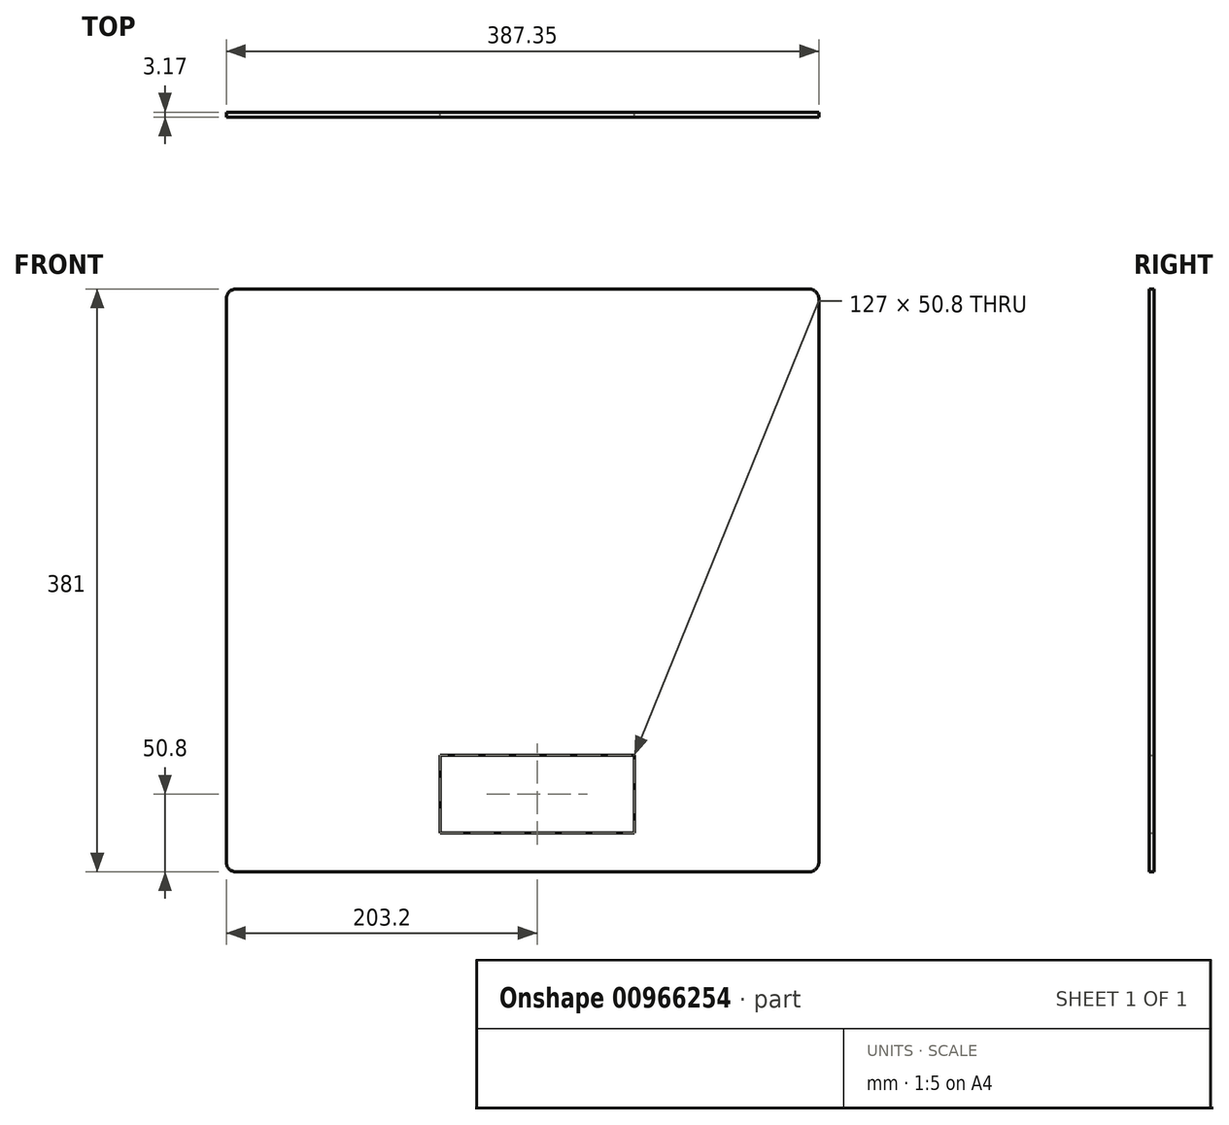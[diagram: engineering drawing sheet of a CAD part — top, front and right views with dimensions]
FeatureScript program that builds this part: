
annotation { "Feature Type Name" : "Feature", "Feature Type Description" : "" }
export const myFeature = defineFeature(function(context is Context, id is Id, definition is map)
    precondition{}
    {
        {
            var Q0;
            Q0=qCreatedBy(makeId("Front.planeOp"),FACE);
            var sketch = newSketch(context, id + "F0", { "sketchPlane" : qUnion([Q0])});
            skLineSegment(sketch, "E0.bottom", {"start": v(6.35, 0) * mm, "end": v(381, 0) * mm});
            skLineSegment(sketch, "E0.top", {"start": v(6.35, 381) * mm, "end": v(381, 381) * mm});
            skLineSegment(sketch, "E0.left", {"start": v(0, 6.35) * mm, "end": v(0, 374.65) * mm});
            skLineSegment(sketch, "E0.right", {"start": v(387.35, 6.35) * mm, "end": v(387.35, 374.65) * mm});
            skPoint(sketch, "E1.visualSharp", {"position": v(0, 381) * mm});
            skArc(sketch, "E1.filletArc", {"start": v(6.35, 381) * mm, "mid": v(1.86, 379.14) * mm, "end": v(0, 374.65) * mm});
            skPoint(sketch, "E2.visualSharp", {"position": v(0, 0) * mm});
            skArc(sketch, "E2.filletArc", {"start": v(0, 6.35) * mm, "mid": v(1.86, 1.86) * mm, "end": v(6.35, 0) * mm});
            skPoint(sketch, "E3.visualSharp", {"position": v(387.35, 0) * mm});
            skArc(sketch, "E3.filletArc", {"start": v(381, 0) * mm, "mid": v(385.5, 1.86) * mm, "end": v(387.35, 6.35) * mm});
            skPoint(sketch, "E4.visualSharp", {"position": v(387.35, 381) * mm});
            skArc(sketch, "E4.filletArc", {"start": v(387.35, 374.65) * mm, "mid": v(385.5, 379.14) * mm, "end": v(381, 381) * mm});
            skLineSegment(sketch, "E5.bottom", {"start": v(139.7, 76.2) * mm, "end": v(266.7, 76.2) * mm});
            skLineSegment(sketch, "E5.top", {"start": v(139.7, 25.4) * mm, "end": v(266.7, 25.4) * mm});
            skLineSegment(sketch, "E5.left", {"start": v(139.7, 76.2) * mm, "end": v(139.7, 25.4) * mm});
            skLineSegment(sketch, "E5.right", {"start": v(266.7, 76.2) * mm, "end": v(266.7, 25.4) * mm});
            skSolve(sketch);
        }
        {
            var Q0;
            Q0=makeQuery(id+"F0.imprint","IMPRINT",FACE,{"disambiguationData":[TD([[makeQuery(id+"F0.imprint","IMPRINT",EDGE,{"derivedFrom":sQuery(id+"F0.wireOp",EDGE,"E0.bottom")}),1.0]])]});
            extrude(context, id + "F1", {"entities" : qUnion([Q0]), "depth" : 3.17 * mm});
        }
    });
